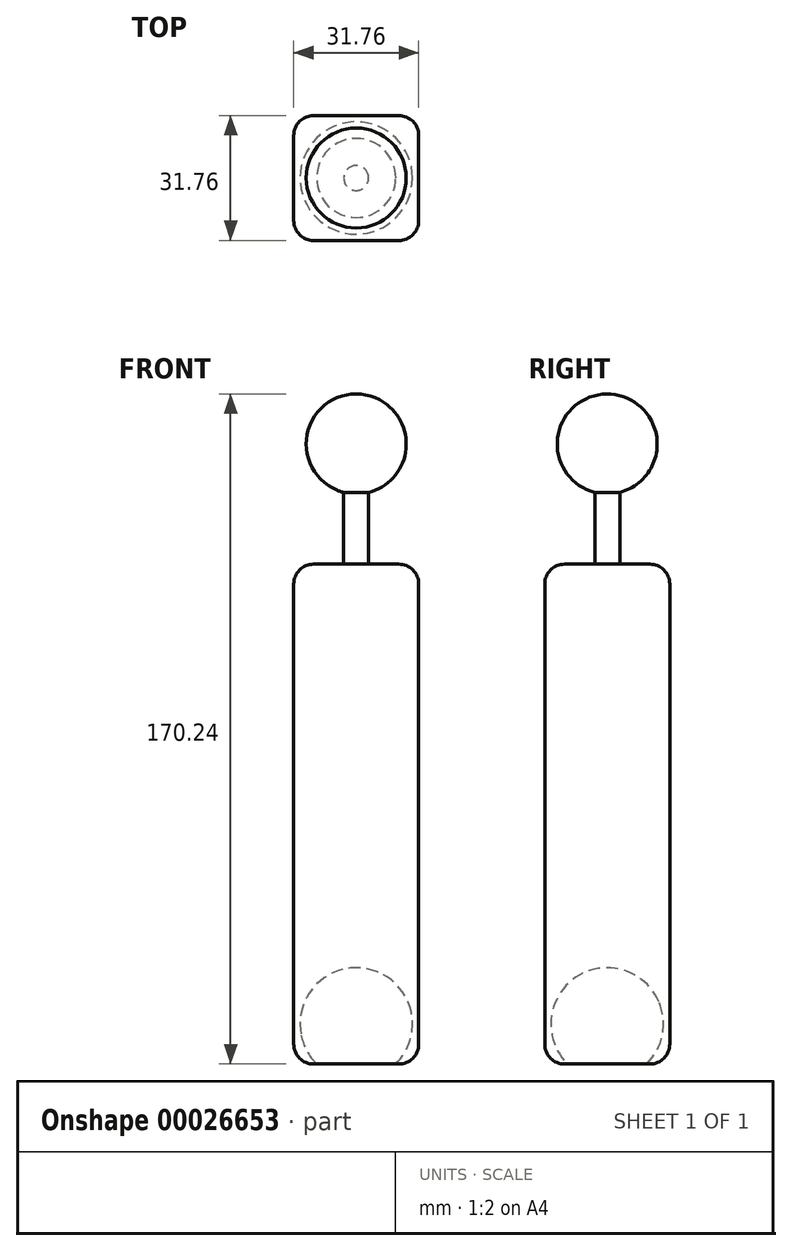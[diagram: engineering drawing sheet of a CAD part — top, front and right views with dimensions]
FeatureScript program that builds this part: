
annotation { "Feature Type Name" : "Feature", "Feature Type Description" : "" }
export const myFeature = defineFeature(function(context is Context, id is Id, definition is map)
    precondition{}
    {
        {
            var Q0;
            Q0=qCreatedBy(makeId("Front.planeOp"),FACE);
            var sketch = newSketch(context, id + "F0", { "sketchPlane" : qUnion([Q0])});
            skLineSegment(sketch, "E0.rect.bottom", {"start": v(-15.87, 63.5) * mm, "end": v(15.88, 63.5) * mm});
            skLineSegment(sketch, "E0.rect.top", {"start": v(-15.88, -63.5) * mm, "end": v(15.87, -63.5) * mm});
            skLineSegment(sketch, "E0.rect.left", {"start": v(-15.87, 63.5) * mm, "end": v(-15.88, -63.5) * mm});
            skLineSegment(sketch, "E0.rect.right", {"start": v(15.88, 63.5) * mm, "end": v(15.87, -63.5) * mm});
            skPoint(sketch, "E0.rect.middle", {"position": v(0, 0) * mm});
            skSolve(sketch);
        }
        {
            var Q0;
            Q0 = qSketchRegion(id + "F0", true);
            extrude(context, id + "F1", {"entities" : qUnion([Q0]), "depth" : 15.88 * mm, "hasSecondDirection" : true, "secondDirectionOppositeDirection" : true, "secondDirectionDepth" : 15.88 * mm});
        }
        {
            var Q0;
            Q0=makeQuery(id+"F1.opExtrude","CAP_EDGE",EDGE,{"disambiguationData":[OSD([sQuery(id+"F0.wireOp",EDGE,"E0.rect.left")])],"isStart":false});
            var Q1;
            Q1=makeQuery(id+"F1.opExtrude","CAP_EDGE",EDGE,{"disambiguationData":[OSD([sQuery(id+"F0.wireOp",EDGE,"E0.rect.right")])],"isStart":false});
            var Q2;
            Q2=makeQuery(id+"F1.opExtrude","CAP_EDGE",EDGE,{"disambiguationData":[OSD([sQuery(id+"F0.wireOp",EDGE,"E0.rect.right")])],"isStart":true});
            var Q3;
            Q3=makeQuery(id+"F1.opExtrude","CAP_EDGE",EDGE,{"disambiguationData":[OSD([sQuery(id+"F0.wireOp",EDGE,"E0.rect.left")])],"isStart":true});
            fillet(context, id + "F2", {"entities" : qUnion([Q0, Q1, Q2, Q3]), "radius" : 5.08 * mm, "tangentPropagation" : true, "allowEdgeOverflow" : false});
        }
        {
            var Q0;
            Q0=makeQuery(id+"F1.opExtrude","SWEPT_FACE",FACE,{"disambiguationData":[OSD([sQuery(id+"F0.wireOp",EDGE,"E0.rect.bottom")])]});
            var sketch = newSketch(context, id + "F3", { "sketchPlane" : qUnion([Q0])});
            skCircle(sketch, "E1", {"center": v(0, 0) * mm, "radius": 3.18 * mm});
            skSolve(sketch);
        }
        {
            var Q0;
            Q0 = qSketchRegion(id + "F3", true);
            extrude(context, id + "F4", {"entities" : qUnion([Q0]), "operationType" : NewBodyOperationType.ADD, "depth" : 38.1 * mm});
        }
        {
            var Q0;
            Q0=qCreatedBy(makeId("Front.planeOp"),FACE);
            var sketch = newSketch(context, id + "F5", { "sketchPlane" : qUnion([Q0])});
            skPoint(sketch, "E2", {"position": v(0, 51.94) * mm});
            skLineSegment(sketch, "E3", {"start": v(-13.83, 54.17) * mm, "end": v(11.57, 54.17) * mm});
            skPoint(sketch, "E4", {"position": v(0, 94.04) * mm});
            skLineSegment(sketch, "E5", {"start": v(-7.05, 83.47) * mm, "end": v(7.05, 104.6) * mm});
            skPoint(sketch, "E6.orphan", {"position": v(12.7, 94.04) * mm});
            skPoint(sketch, "E7.start.orphan", {"position": v(-12.7, 94.04) * mm});
            skArc(sketch, "E8", {"start": v(7.05, 104.6) * mm, "mid": v(-10.56, 101.08) * mm, "end": v(-7.05, 83.47) * mm});
            skSolve(sketch);
        }
        {
            var Q0;
            Q0 = qSketchRegion(id + "F5", true);
            var Q1;
            Q1=sQuery(id+"F5.wireOp",EDGE,"E5");
            revolve(context, id + "F6", {"operationType" : NewBodyOperationType.ADD, "entities" : qUnion([Q0]), "axis" : qUnion([Q1]), "revolveType" : RevolveType.FULL});
        }
        {
            var Q0;
            Q0=qCreatedBy(makeId("Front.planeOp"),FACE);
            var sketch = newSketch(context, id + "F7", { "sketchPlane" : qUnion([Q0])});
            skPoint(sketch, "E9", {"position": v(0, -63.5) * mm});
            skPoint(sketch, "E10", {"position": v(0, -58.42) * mm});
            skPoint(sketch, "E11", {"position": v(0, -53.34) * mm});
            skArc(sketch, "E12", {"start": v(-13.98, -56.27) * mm, "mid": v(2.93, -67.32) * mm, "end": v(13.98, -50.4) * mm});
            skLineSegment(sketch, "E13", {"start": v(13.98, -50.4) * mm, "end": v(0, -53.34) * mm});
            skLineSegment(sketch, "E14", {"start": v(0, -53.34) * mm, "end": v(-13.98, -56.27) * mm});
            skLineSegment(sketch, "E15", {"start": v(13.98, -50.4) * mm, "end": v(-13.98, -56.27) * mm});
            skLineSegment(sketch, "E16", {"start": v(0, -63.5) * mm, "end": v(0, -67.63) * mm});
            skSolve(sketch);
        }
        {
            var Q0;
            Q0 = qSketchRegion(id + "F7", true);
            var Q1;
            Q1=sQuery(id+"F7.wireOp",EDGE,"E15");
            revolve(context, id + "F8", {"operationType" : NewBodyOperationType.REMOVE, "entities" : qUnion([Q0]), "axis" : qUnion([Q1]), "revolveType" : RevolveType.FULL, "oppositeDirection" : true});
        }
        {
            var Q0;
            Q0=makeQuery(id+"F1.opExtrude","CAP_EDGE",EDGE,{"disambiguationData":[OSD([sQuery(id+"F0.wireOp",EDGE,"E0.rect.bottom")])],"isStart":true});
            var Q1;
            Q1=makeQuery(id+"F1.opExtrude","SWEPT_EDGE",EDGE,{"disambiguationData":[OSD([sQuery(id+"F0.wireOp",EDGE,"E0.rect.bottom"),sQuery(id+"F0.wireOp",EDGE,"E0.rect.right")])]});
            var Q2;
            Q2=makeQuery(id+"F1.opExtrude","SWEPT_EDGE",EDGE,{"disambiguationData":[OSD([sQuery(id+"F0.wireOp",EDGE,"E0.rect.bottom"),sQuery(id+"F0.wireOp",EDGE,"E0.rect.left")])]});
            var Q3;
            Q3=makeQuery(id+"F2.opFillet","BLEND_EDGE",EDGE,{"blendedFrom":[makeQuery(id+"F1.opExtrude","CAP_EDGE",EDGE,{"disambiguationData":[OSD([sQuery(id+"F0.wireOp",EDGE,"E0.rect.left")])],"isStart":true}),makeQuery(id+"F1.opExtrude","SWEPT_FACE",FACE,{"disambiguationData":[OSD([sQuery(id+"F0.wireOp",EDGE,"E0.rect.bottom")])]})],"blendedInto":[makeQuery(id+"F1.opExtrude","SWEPT_FACE",FACE,{"disambiguationData":[OSD([sQuery(id+"F0.wireOp",EDGE,"E0.rect.bottom")])]})]});
            var Q4;
            Q4=makeQuery(id+"F2.opFillet","BLEND_EDGE",EDGE,{"blendedFrom":[makeQuery(id+"F1.opExtrude","CAP_EDGE",EDGE,{"disambiguationData":[OSD([sQuery(id+"F0.wireOp",EDGE,"E0.rect.right")])],"isStart":true}),makeQuery(id+"F1.opExtrude","SWEPT_FACE",FACE,{"disambiguationData":[OSD([sQuery(id+"F0.wireOp",EDGE,"E0.rect.bottom")])]})],"blendedInto":[makeQuery(id+"F1.opExtrude","SWEPT_FACE",FACE,{"disambiguationData":[OSD([sQuery(id+"F0.wireOp",EDGE,"E0.rect.bottom")])]})]});
            var Q5;
            Q5=makeQuery(id+"F2.opFillet","BLEND_EDGE",EDGE,{"blendedFrom":[makeQuery(id+"F1.opExtrude","CAP_EDGE",EDGE,{"disambiguationData":[OSD([sQuery(id+"F0.wireOp",EDGE,"E0.rect.right")])],"isStart":false}),makeQuery(id+"F1.opExtrude","SWEPT_FACE",FACE,{"disambiguationData":[OSD([sQuery(id+"F0.wireOp",EDGE,"E0.rect.bottom")])]})],"blendedInto":[makeQuery(id+"F1.opExtrude","SWEPT_FACE",FACE,{"disambiguationData":[OSD([sQuery(id+"F0.wireOp",EDGE,"E0.rect.bottom")])]})]});
            var Q6;
            Q6=makeQuery(id+"F1.opExtrude","CAP_EDGE",EDGE,{"disambiguationData":[OSD([sQuery(id+"F0.wireOp",EDGE,"E0.rect.bottom")])],"isStart":false});
            var Q7;
            Q7=makeQuery(id+"F2.opFillet","BLEND_EDGE",EDGE,{"blendedFrom":[makeQuery(id+"F1.opExtrude","CAP_EDGE",EDGE,{"disambiguationData":[OSD([sQuery(id+"F0.wireOp",EDGE,"E0.rect.left")])],"isStart":false}),makeQuery(id+"F1.opExtrude","SWEPT_FACE",FACE,{"disambiguationData":[OSD([sQuery(id+"F0.wireOp",EDGE,"E0.rect.bottom")])]})],"blendedInto":[makeQuery(id+"F1.opExtrude","SWEPT_FACE",FACE,{"disambiguationData":[OSD([sQuery(id+"F0.wireOp",EDGE,"E0.rect.bottom")])]})]});
            var Q8;
            Q8=makeQuery(id+"F1.opExtrude","SWEPT_EDGE",EDGE,{"disambiguationData":[OSD([sQuery(id+"F0.wireOp",EDGE,"E0.rect.top"),sQuery(id+"F0.wireOp",EDGE,"E0.rect.right")])]});
            var Q9;
            Q9=makeQuery(id+"F2.opFillet","BLEND_EDGE",EDGE,{"blendedFrom":[makeQuery(id+"F1.opExtrude","CAP_EDGE",EDGE,{"disambiguationData":[OSD([sQuery(id+"F0.wireOp",EDGE,"E0.rect.right")])],"isStart":false}),makeQuery(id+"F1.opExtrude","SWEPT_FACE",FACE,{"disambiguationData":[OSD([sQuery(id+"F0.wireOp",EDGE,"E0.rect.top")])]})],"blendedInto":[makeQuery(id+"F1.opExtrude","SWEPT_FACE",FACE,{"disambiguationData":[OSD([sQuery(id+"F0.wireOp",EDGE,"E0.rect.top")])]})]});
            var Q10;
            Q10=makeQuery(id+"F1.opExtrude","CAP_EDGE",EDGE,{"disambiguationData":[OSD([sQuery(id+"F0.wireOp",EDGE,"E0.rect.top")])],"isStart":false});
            var Q11;
            Q11=makeQuery(id+"F2.opFillet","BLEND_EDGE",EDGE,{"blendedFrom":[makeQuery(id+"F1.opExtrude","CAP_EDGE",EDGE,{"disambiguationData":[OSD([sQuery(id+"F0.wireOp",EDGE,"E0.rect.left")])],"isStart":false}),makeQuery(id+"F1.opExtrude","SWEPT_FACE",FACE,{"disambiguationData":[OSD([sQuery(id+"F0.wireOp",EDGE,"E0.rect.top")])]})],"blendedInto":[makeQuery(id+"F1.opExtrude","SWEPT_FACE",FACE,{"disambiguationData":[OSD([sQuery(id+"F0.wireOp",EDGE,"E0.rect.top")])]})]});
            var Q12;
            Q12=makeQuery(id+"F1.opExtrude","SWEPT_EDGE",EDGE,{"disambiguationData":[OSD([sQuery(id+"F0.wireOp",EDGE,"E0.rect.top"),sQuery(id+"F0.wireOp",EDGE,"E0.rect.left")])]});
            var Q13;
            Q13=makeQuery(id+"F1.opExtrude","CAP_EDGE",EDGE,{"disambiguationData":[OSD([sQuery(id+"F0.wireOp",EDGE,"E0.rect.top")])],"isStart":true});
            var Q14;
            Q14=makeQuery(id+"F2.opFillet","BLEND_EDGE",EDGE,{"blendedFrom":[makeQuery(id+"F1.opExtrude","CAP_EDGE",EDGE,{"disambiguationData":[OSD([sQuery(id+"F0.wireOp",EDGE,"E0.rect.left")])],"isStart":true}),makeQuery(id+"F1.opExtrude","SWEPT_FACE",FACE,{"disambiguationData":[OSD([sQuery(id+"F0.wireOp",EDGE,"E0.rect.top")])]})],"blendedInto":[makeQuery(id+"F1.opExtrude","SWEPT_FACE",FACE,{"disambiguationData":[OSD([sQuery(id+"F0.wireOp",EDGE,"E0.rect.top")])]})]});
            var Q15;
            Q15=makeQuery(id+"F2.opFillet","BLEND_EDGE",EDGE,{"blendedFrom":[makeQuery(id+"F1.opExtrude","CAP_EDGE",EDGE,{"disambiguationData":[OSD([sQuery(id+"F0.wireOp",EDGE,"E0.rect.right")])],"isStart":true}),makeQuery(id+"F1.opExtrude","SWEPT_FACE",FACE,{"disambiguationData":[OSD([sQuery(id+"F0.wireOp",EDGE,"E0.rect.top")])]})],"blendedInto":[makeQuery(id+"F1.opExtrude","SWEPT_FACE",FACE,{"disambiguationData":[OSD([sQuery(id+"F0.wireOp",EDGE,"E0.rect.top")])]})]});
            fillet(context, id + "F9", {"entities" : qUnion([Q0, Q1, Q2, Q3, Q4, Q5, Q6, Q7, Q8, Q9, Q10, Q11, Q12, Q13, Q14, Q15]), "radius" : 5.08 * mm, "tangentPropagation" : true, "allowEdgeOverflow" : false});
        }
    });
